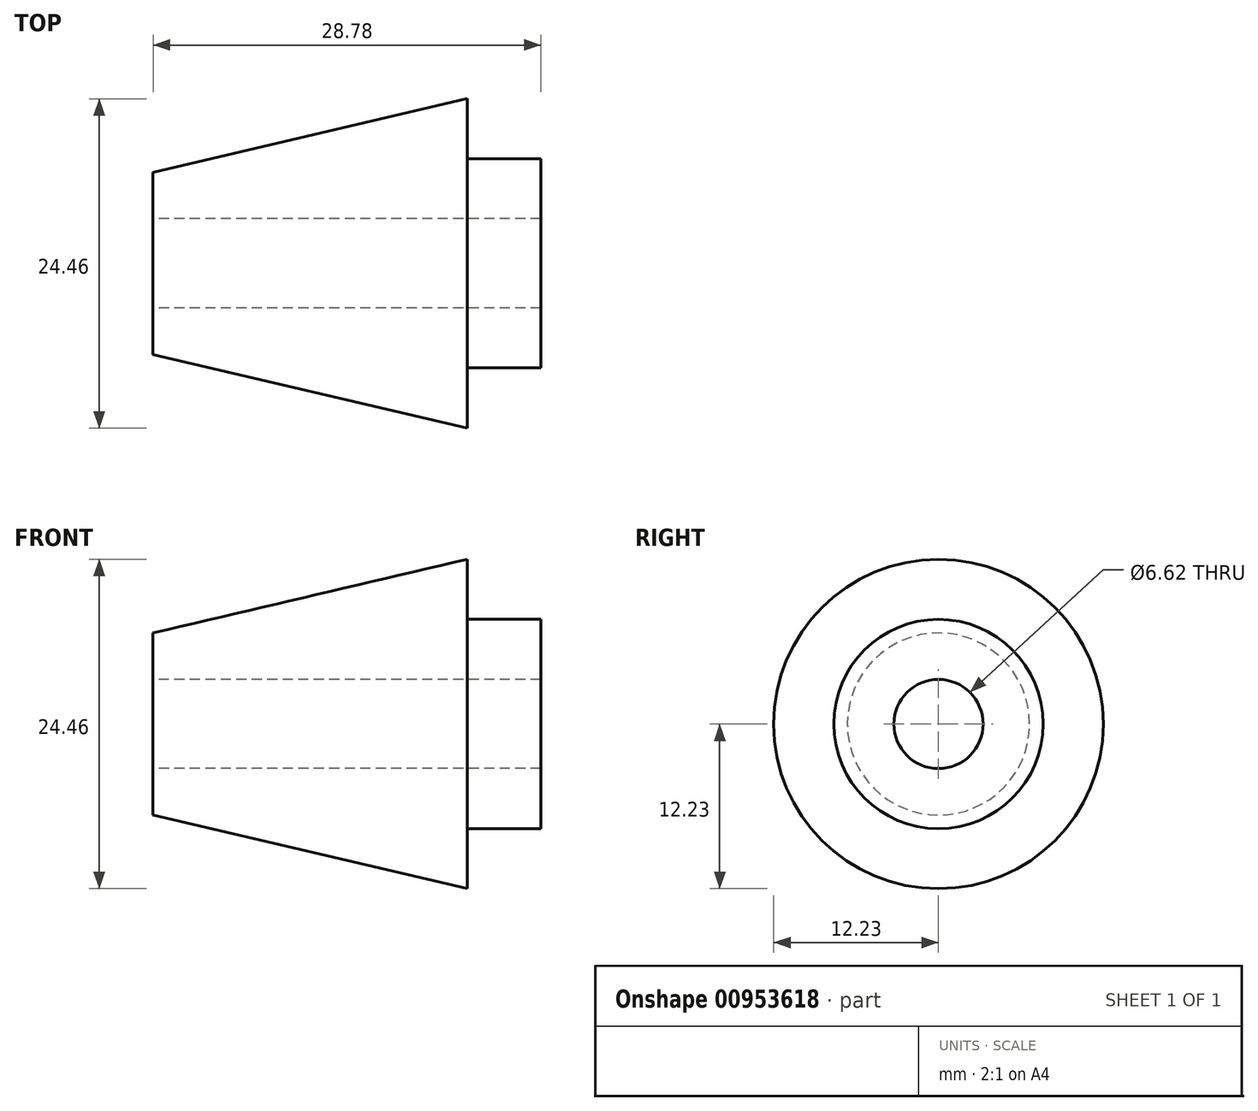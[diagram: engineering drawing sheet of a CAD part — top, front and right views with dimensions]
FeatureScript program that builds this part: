
annotation { "Feature Type Name" : "Feature", "Feature Type Description" : "" }
export const myFeature = defineFeature(function(context is Context, id is Id, definition is map)
    precondition{}
    {
        {
            var Q0;
            Q0=qCreatedBy(makeId("Front.planeOp"),FACE);
            var sketch = newSketch(context, id + "F0", { "sketchPlane" : qUnion([Q0])});
            skLineSegment(sketch, "E0", {"start": v(-10.5, 3.3) * mm, "end": v(12.8, 3.3) * mm});
            skLineSegment(sketch, "E1", {"start": v(12.8, 12.23) * mm, "end": v(-10.5, 6.76) * mm});
            skLineSegment(sketch, "E2", {"start": v(-10.5, 6.76) * mm, "end": v(-10.5, 3.3) * mm});
            skPoint(sketch, "E3.startSnap0", {"position": v(12.8, 7.77) * mm});
            skPoint(sketch, "E3.startSnap1", {"position": v(1.15, 9.5) * mm});
            skLineSegment(sketch, "E4", {"start": v(-20.58, 0) * mm, "end": v(32.67, 0) * mm});
            skPoint(sketch, "E3.start.orphan", {"position": v(12.8, 9.5) * mm});
            skPoint(sketch, "E5.end.orphan", {"position": v(18.28, 3.3) * mm});
            skLineSegment(sketch, "E6", {"start": v(12.8, 12.23) * mm, "end": v(12.8, 7.77) * mm});
            skLineSegment(sketch, "E7", {"start": v(12.8, 7.77) * mm, "end": v(18.28, 7.77) * mm});
            skLineSegment(sketch, "E8", {"start": v(18.28, 7.77) * mm, "end": v(18.28, 3.3) * mm});
            skLineSegment(sketch, "E9", {"start": v(18.28, 3.3) * mm, "end": v(12.8, 3.3) * mm});
            skSolve(sketch);
        }
        {
            var Q0;
            Q0=makeQuery(id+"F0.imprint","IMPRINT",FACE,{"disambiguationData":[TD([[makeQuery(id+"F0.imprint","IMPRINT",EDGE,{"derivedFrom":sQuery(id+"F0.wireOp",EDGE,"E0")}),1.0]])]});
            var Q1;
            Q1=sQuery(id+"F0.wireOp",EDGE,"E4");
            revolve(context, id + "F1", {"surfaceOperationType" : NewSurfaceOperationType.NEW, "entities" : qUnion([Q0]), "axis" : qUnion([Q1]), "revolveType" : RevolveType.FULL});
        }
    });
